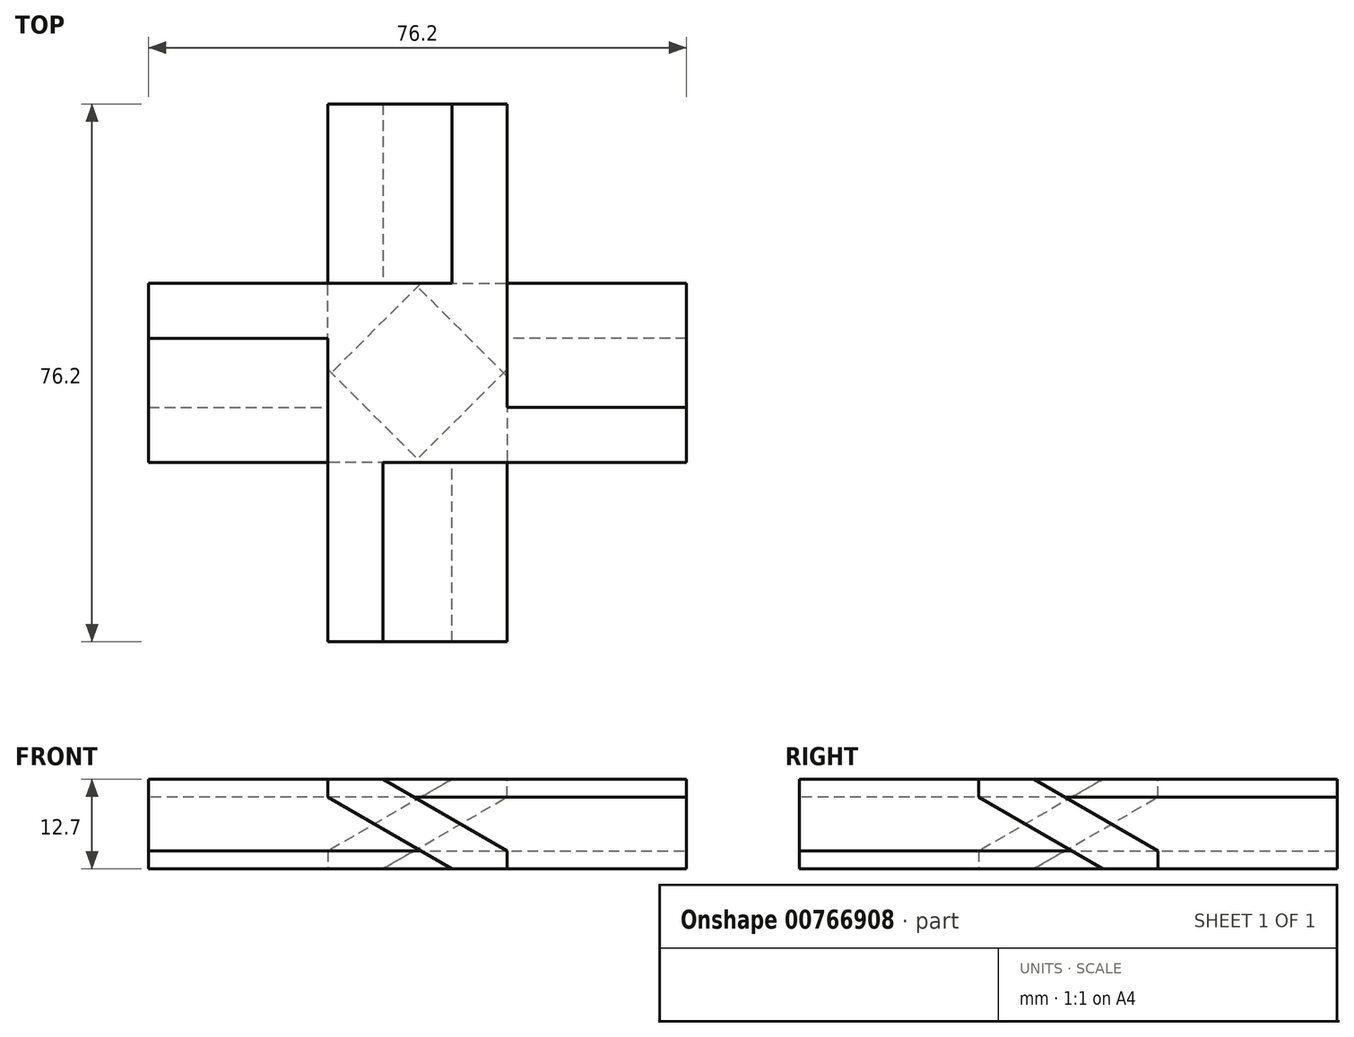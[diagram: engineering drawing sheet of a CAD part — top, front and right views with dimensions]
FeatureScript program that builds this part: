
annotation { "Feature Type Name" : "Feature", "Feature Type Description" : "" }
export const myFeature = defineFeature(function(context is Context, id is Id, definition is map)
    precondition{}
    {
        {
            var Q0;
            Q0=qCreatedBy(makeId("Top.planeOp"),FACE);
            var sketch = newSketch(context, id + "F0", { "sketchPlane" : qUnion([Q0])});
            skPoint(sketch, "E0.middle", {"position": v(0, 0) * mm});
            skLineSegment(sketch, "E1.top", {"start": v(-12.7, 38.1) * mm, "end": v(12.7, 38.1) * mm});
            skLineSegment(sketch, "E1.left", {"start": v(-12.7, 12.7) * mm, "end": v(-12.7, 38.1) * mm});
            skLineSegment(sketch, "E1.right", {"start": v(12.7, 12.7) * mm, "end": v(12.7, 38.1) * mm});
            skLineSegment(sketch, "E2.bottom", {"start": v(12.7, 12.7) * mm, "end": v(38.1, 12.7) * mm});
            skLineSegment(sketch, "E2.top", {"start": v(12.7, -12.7) * mm, "end": v(38.1, -12.7) * mm});
            skLineSegment(sketch, "E2.right", {"start": v(38.1, 12.7) * mm, "end": v(38.1, -12.7) * mm});
            skLineSegment(sketch, "E3.top", {"start": v(12.7, -38.1) * mm, "end": v(-12.7, -38.1) * mm});
            skLineSegment(sketch, "E3.left", {"start": v(12.7, -12.7) * mm, "end": v(12.7, -38.1) * mm});
            skLineSegment(sketch, "E3.right", {"start": v(-12.7, -12.7) * mm, "end": v(-12.7, -38.1) * mm});
            skLineSegment(sketch, "E4.bottom", {"start": v(-12.7, -12.7) * mm, "end": v(-38.1, -12.7) * mm});
            skLineSegment(sketch, "E4.top", {"start": v(-12.7, 12.7) * mm, "end": v(-38.1, 12.7) * mm});
            skLineSegment(sketch, "E4.right", {"start": v(-38.1, -12.7) * mm, "end": v(-38.1, 12.7) * mm});
            skSolve(sketch);
        }
        {
            var Q0;
            Q0 = qSketchRegion(id + "F0", true);
            extrude(context, id + "F1", {"entities" : qUnion([Q0]), "depth" : 12.7 * mm, "offsetDistance" : 25.4 * mm});
        }
        {
            var Q0;
            Q0=makeQuery(id+"F1.opExtrude","CAP_EDGE",EDGE,{"disambiguationData":[OSD([sQuery(id+"F0.wireOp",EDGE,"E3.right")])],"isStart":true});
            var Q1;
            Q1=makeQuery(id+"F1.opExtrude","CAP_EDGE",EDGE,{"disambiguationData":[OSD([sQuery(id+"F0.wireOp",EDGE,"E3.left")])],"isStart":false});
            chamfer(context, id + "F2", {"entities" : qUnion([Q0, Q1]), "chamferType" : ChamferType.OFFSET_ANGLE, "width" : 10.16 * mm, "oppositeDirection" : false, "angle" : 60 * degree, "tangentPropagation" : true});
        }
        {
            var Q0;
            Q0=makeQuery(id+"F1.opExtrude","CAP_EDGE",EDGE,{"disambiguationData":[OSD([sQuery(id+"F0.wireOp",EDGE,"E4.bottom")])],"isStart":false});
            var Q1;
            Q1=makeQuery(id+"F1.opExtrude","CAP_EDGE",EDGE,{"disambiguationData":[OSD([sQuery(id+"F0.wireOp",EDGE,"E4.top")])],"isStart":true});
            var Q2;
            Q2=makeQuery(id+"F1.opExtrude","CAP_EDGE",EDGE,{"disambiguationData":[OSD([sQuery(id+"F0.wireOp",EDGE,"E1.right")])],"isStart":true});
            var Q3;
            Q3=makeQuery(id+"F1.opExtrude","CAP_EDGE",EDGE,{"disambiguationData":[OSD([sQuery(id+"F0.wireOp",EDGE,"E2.top")])],"isStart":true});
            chamfer(context, id + "F3", {"entities" : qUnion([Q0, Q1, Q2, Q3]), "chamferType" : ChamferType.OFFSET_ANGLE, "width" : 10.16 * mm, "oppositeDirection" : false, "angle" : 60 * degree, "tangentPropagation" : true});
        }
        {
            var Q0;
            Q0=makeQuery(id+"F1.opExtrude","CAP_EDGE",EDGE,{"disambiguationData":[OSD([sQuery(id+"F0.wireOp",EDGE,"E1.left")])],"isStart":false});
            var Q1;
            Q1=makeQuery(id+"F1.opExtrude","CAP_EDGE",EDGE,{"disambiguationData":[OSD([sQuery(id+"F0.wireOp",EDGE,"E2.bottom")])],"isStart":false});
            chamfer(context, id + "F4", {"entities" : qUnion([Q0, Q1]), "chamferType" : ChamferType.OFFSET_ANGLE, "width" : 10.16 * mm, "oppositeDirection" : false, "angle" : 60 * degree, "tangentPropagation" : true});
        }
    });
